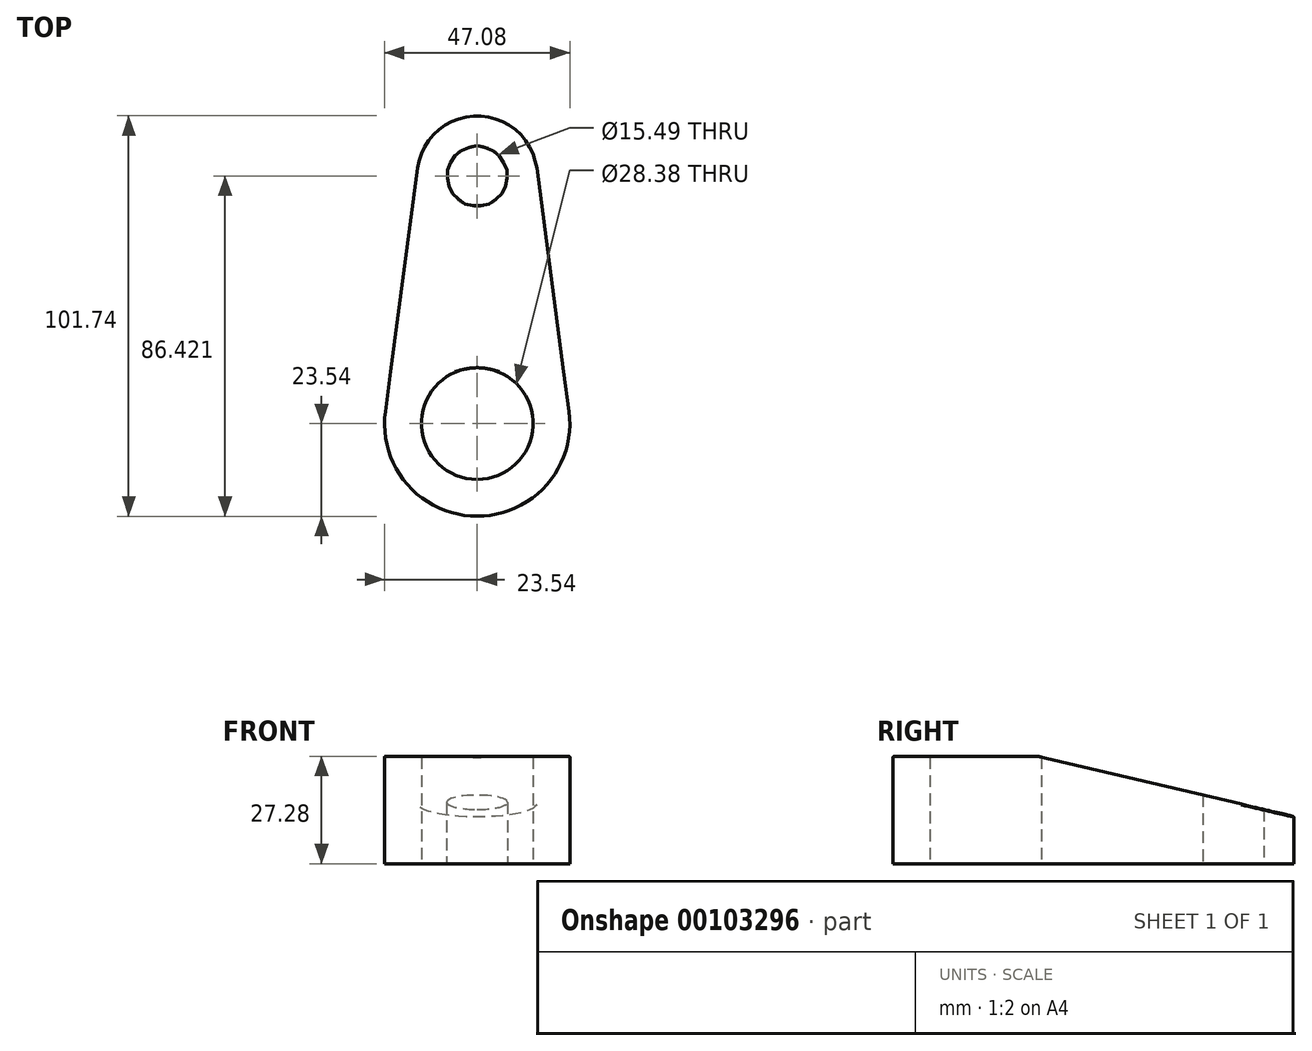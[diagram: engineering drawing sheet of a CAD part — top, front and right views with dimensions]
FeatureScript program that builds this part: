
annotation { "Feature Type Name" : "Feature", "Feature Type Description" : "" }
export const myFeature = defineFeature(function(context is Context, id is Id, definition is map)
    precondition{}
    {
        {
            var Q0;
            Q0=qCreatedBy(makeId("Top.planeOp"),FACE);
            var sketch = newSketch(context, id + "F0", { "sketchPlane" : qUnion([Q0])});
            skCircle(sketch, "E0", {"center": v(0, 0) * mm, "radius": 14.19 * mm});
            skCircle(sketch, "E1", {"center": v(0, 0) * mm, "radius": 23.54 * mm});
            skCircle(sketch, "E2", {"center": v(0, 62.88) * mm, "radius": 7.74 * mm});
            skCircle(sketch, "E3", {"center": v(0, 62.88) * mm, "radius": 15.32 * mm});
            skLineSegment(sketch, "E4", {"start": v(-23.34, 3.08) * mm, "end": v(-15.19, 64.88) * mm});
            skLineSegment(sketch, "E5", {"start": v(23.34, 3.08) * mm, "end": v(15.19, 64.88) * mm});
            skSolve(sketch);
        }
        {
            var Q0;
            {var subQ0=sQuery(id+"F0.wireOp",EDGE,"E4");Q0=makeQuery(id+"F0.imprint","IMPRINT",FACE,{"disambiguationData":[TD([[makeQuery(id+"F0.imprint","IMPRINT",EDGE,{"derivedFrom":subQ0}),-1.0]])]});}
            var Q1;
            Q1=makeQuery(id+"F0.imprint","IMPRINT",FACE,{"disambiguationData":[TD([[makeQuery(id+"F0.imprint","IMPRINT",EDGE,{"derivedFrom":sQuery(id+"F0.wireOp",EDGE,"E0")}),-1.0]])]});
            var Q2;
            Q2=makeQuery(id+"F0.imprint","IMPRINT",FACE,{"disambiguationData":[TD([[makeQuery(id+"F0.imprint","IMPRINT",EDGE,{"derivedFrom":sQuery(id+"F0.wireOp",EDGE,"E2")}),-1.0]])]});
            extrude(context, id + "F1", {"entities" : qUnion([Q0, Q1, Q2]), "depth" : 27.28 * mm});
        }
        {
            var Q0;
            Q0=qCreatedBy(makeId("Right.planeOp"),FACE);
            var sketch = newSketch(context, id + "F2", { "sketchPlane" : qUnion([Q0])});
            skLineSegment(sketch, "E6", {"start": v(0, 0) * mm, "end": v(0, 26.99) * mm, "construction": true});
            skSolve(sketch);
        }
        {
            var Q0;
            Q0=qCreatedBy(makeId("Right.planeOp"),FACE);
            var sketch = newSketch(context, id + "F3", { "sketchPlane" : qUnion([Q0])});
            skLineSegment(sketch, "E7", {"start": v(12.1, 27.55) * mm, "end": v(98.72, 27.55) * mm});
            skLineSegment(sketch, "E8", {"start": v(98.72, 27.55) * mm, "end": v(98.72, 7.18) * mm});
            skLineSegment(sketch, "E9", {"start": v(98.72, 7.18) * mm, "end": v(12.1, 27.55) * mm});
            skSolve(sketch);
        }
        {
            var Q0;
            Q0 = qSketchRegion(id + "F3", true);
            extrude(context, id + "F4", {"entities" : qUnion([Q0]), "operationType" : NewBodyOperationType.REMOVE, "depth" : 70.83 * mm, "hasSecondDirection" : true, "secondDirectionOppositeDirection" : true, "secondDirectionDepth" : 25.4 * mm});
        }
        {
            var Q0;
            Q0=makeQuery(id+"F1.opExtrude","CAP_EDGE",EDGE,{"disambiguationData":[OSD([sQuery(id+"F0.wireOp",EDGE,"E0")])],"isStart":false});
            var Q1;
            Q1=makeQuery(id+"F1.opExtrude","CAP_EDGE",EDGE,{"disambiguationData":[OSD([sQuery(id+"F0.wireOp",EDGE,"E1")])],"isStart":false});
            var Q2;
            Q2=makeQuery(id+"F4.boolean.opBoolean","INTERSECT",EDGE,{"derivedFrom":[makeQuery(id+"F1.opExtrude","SWEPT_FACE",FACE,{"disambiguationData":[OSD([sQuery(id+"F0.wireOp",EDGE,"E5")])]}),makeQuery(id+"F4.opExtrude","SWEPT_FACE",FACE,{"disambiguationData":[OSD([sQuery(id+"F3.wireOp",EDGE,"E9")])]})]});
            var Q3;
            Q3=makeQuery(id+"F4.boolean.opBoolean","INTERSECT",EDGE,{"disambiguationData":[OD(0.0)],"derivedFrom":[makeQuery(id+"F1.opExtrude","CAP_FACE",FACE,{"disambiguationData":[OSD([sQuery(id+"F0.wireOp",EDGE,"E0"),sQuery(id+"F0.wireOp",EDGE,"E1"),sQuery(id+"F0.wireOp",EDGE,"E2"),sQuery(id+"F0.wireOp",EDGE,"E3"),sQuery(id+"F0.wireOp",EDGE,"E4"),sQuery(id+"F0.wireOp",EDGE,"E5")])],"isStart":false}),makeQuery(id+"F4.opExtrude","SWEPT_FACE",FACE,{"disambiguationData":[OSD([sQuery(id+"F3.wireOp",EDGE,"E9")])]})]});
            var Q4;
            Q4=makeQuery(id+"F4.boolean.opBoolean","INTERSECT",EDGE,{"disambiguationData":[OD(1.0)],"derivedFrom":[makeQuery(id+"F1.opExtrude","CAP_FACE",FACE,{"disambiguationData":[OSD([sQuery(id+"F0.wireOp",EDGE,"E0"),sQuery(id+"F0.wireOp",EDGE,"E1"),sQuery(id+"F0.wireOp",EDGE,"E2"),sQuery(id+"F0.wireOp",EDGE,"E3"),sQuery(id+"F0.wireOp",EDGE,"E4"),sQuery(id+"F0.wireOp",EDGE,"E5")])],"isStart":false}),makeQuery(id+"F4.opExtrude","SWEPT_FACE",FACE,{"disambiguationData":[OSD([sQuery(id+"F3.wireOp",EDGE,"E9")])]})]});
            fillet(context, id + "F5", {"entities" : qUnion([Q0, Q1, Q2, Q3, Q4]), "radius" : 0.2 * mm, "tangentPropagation" : true, "allowEdgeOverflow" : false});
        }
    });
